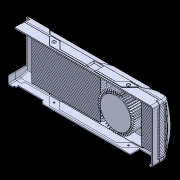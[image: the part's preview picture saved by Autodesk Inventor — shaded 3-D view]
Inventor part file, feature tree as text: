
AUTODESK INVENTOR PART (.ipt)
format: ipt  version: 2018.2 (Build 222227000, 227)  size: 5,883,904 bytes
history: native  units: mm
features: other x62, fillet x1
ambient origin geometry x8: Origin, YZ Plane, XZ Plane, XY Plane, X Axis, Y Axis, Z Axis, Center Point
bodies: Body1 (feature_tree), Body2 (feature_tree), Body3 (feature_tree), Body4 (feature_tree), Body5 (feature_tree), Body6 (feature_tree), Body7 (feature_tree), Body8 (feature_tree), Body9 (feature_tree), Body10 (feature_tree), Body11 (feature_tree), Body12 (feature_tree), Body13 (feature_tree), Body14 (feature_tree), Body15 (feature_tree), Body16 (feature_tree), Body17 (feature_tree), Body18 (feature_tree), Body19 (feature_tree), Body20 (feature_tree), Body21 (feature_tree), Body22 (feature_tree), Body23 (feature_tree), Body24 (feature_tree), Body25 (feature_tree), Body26 (feature_tree), Body27 (feature_tree), Body28 (feature_tree), Body29 (feature_tree), Body30 (feature_tree), Body31 (feature_tree), Body32 (feature_tree)
feature tree (63):
  other  "ソリッド1"
  other  "ソリッド2"
  other  "ソリッド3"
  other  "ソリッド4"
  other  "ソリッド5"
  other  "ソリッド6"
  other  "ソリッド7"
  other  "ソリッド8"
  other  "ソリッド9"
  other  "ソリッド10"
  other  "ソリッド11"
  other  "ソリッド12"
  other  "ソリッド13"
  other  "ソリッド14"
  other  "ソリッド15"
  other  "ソリッド16"
  other  "ソリッド17"
  other  "ソリッド18"
  other  "ソリッド19"
  other  "ソリッド20"
  other  "ソリッド21"
  other  "ソリッド22"
  other  "ソリッド23"
  other  "ソリッド24"
  other  "ソリッド25"
  other  "ソリッド26"
  other  "ソリッド27"
  other  "ソリッド28"
  other  "ソリッド29"
  other  "ソリッド30"
  other  "ソリッド31"
  other  "ソリッド32"
  other  "Cut-Extrude15[1]"
  other  "Cut-Extrude15[2]"
  other  "Cut-Extrude15[3]"
  other  "Cut-Extrude15[4]"
  other  "Cut-Extrude15[5]"
  other  "Cut-Extrude15[6]"
  other  "Cut-Extrude15[7]"
  other  "Cut-Extrude15[8]"
  other  "Cut-Extrude15[9]"
  other  "Cut-Extrude15[10]"
  other  "Boss-Extrude15[1]"
  other  "Boss-Extrude15[2]"
  other  "Boss-Extrude15[3]"
  other  "Boss-Extrude15[4]"
  other  "Boss-Extrude15[5]"
  other  "Boss-Extrude15[6]"
  other  "Boss-Extrude15[7]"
  other  "Boss-Extrude15[8]"
  other  "Boss-Extrude15[9]"
  other  "Boss-Extrude15[10]"
  other  "fan blade"
  other  "fan center metal"
  other  "heatsink large"
  other  "heatsink small"
  other  "nvidia logo"
  fillet  "Fillet49"  [1 undecoded]
  other  "bottom metal"
  other  "top metal"
  other  "window"
  other  "titan text"
  other  "bottom black"
note: 1 required parameter value undecoded (feature->parameter linkage not recoverable at this tier; creation-order binding heuristic only, values carry confidence <= 0.55)
